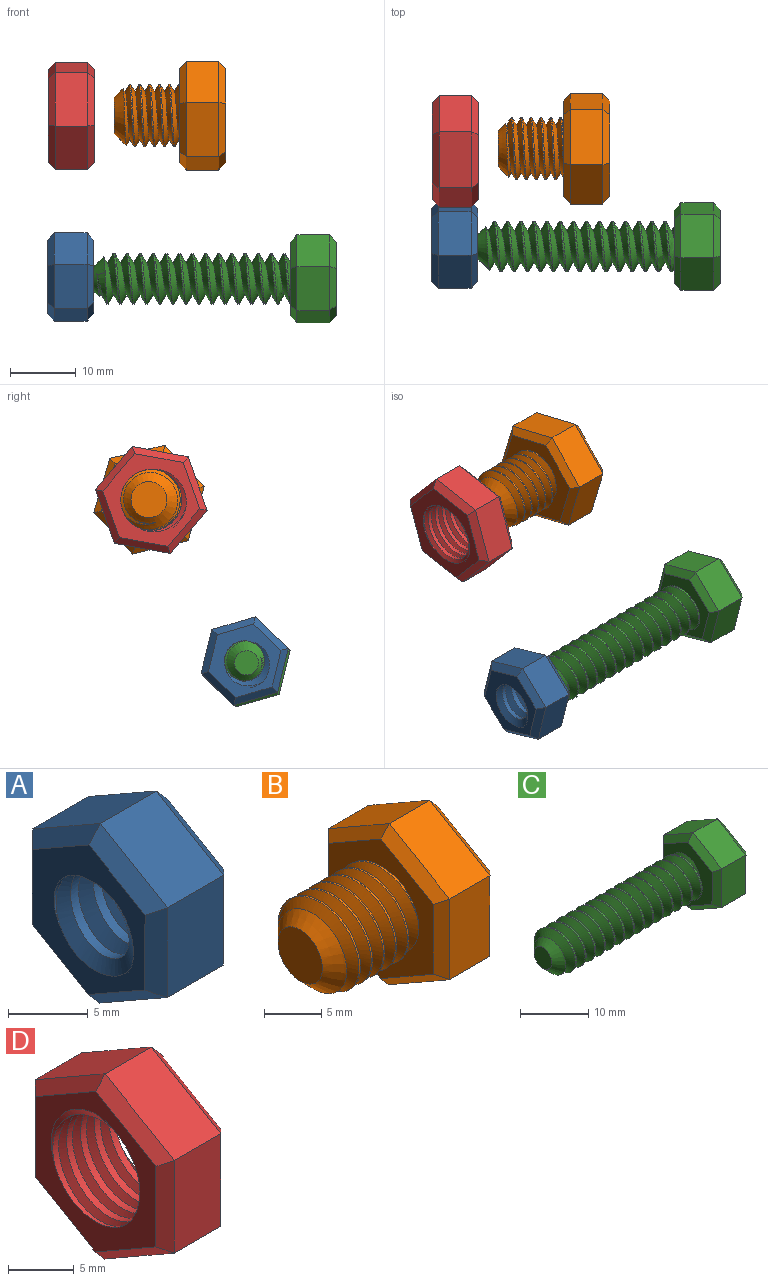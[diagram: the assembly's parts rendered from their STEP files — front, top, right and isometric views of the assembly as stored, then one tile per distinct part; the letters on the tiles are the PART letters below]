
ASSEMBLY  parts=4 mates=2
PART A: 23 faces, bbox 9.2x12.6x14.4 mm
  f0: cylinder r=3.08mm len=7mm, axis (1,0,0), area 47.4mm2, adj f7,f8,f21,f22
  f1: plane 6.02x5mm, normal (0,0.5,0.87), area 34.6mm2, adj f2,f6,f13,f20
  f2: plane 5.98x5mm, normal (0,-0.5,0.86), area 34.6mm2, adj f1,f3,f14,f18
  f3: plane 6.93x5mm, normal (0,-1,-0.01), area 34.6mm2, adj f2,f4,f12,f16
  f4: plane 6.02x5mm, normal (0,-0.5,-0.87), area 34.6mm2, adj f3,f5,f10,f15
  f5: plane 5.98x5mm, normal (0,0.5,-0.86), area 34.6mm2, adj f4,f6,f9,f17
  f6: plane 6.93x5mm, normal (0,1,0.01), area 34.6mm2, adj f1,f5,f11,f19
  f7: plane 12.14x10.62mm, normal (-1,0,0), area 48.9mm2, adj f0,f9,f10,f11,f12,f13,f14,f21
  f8: plane 12.14x10.62mm, normal (1,0,0), area 48.9mm2, adj f0,f15,f16,f17,f18,f19,f20,f21
  f9: plane 5.99x4.07mm, normal (-0.71,0.36,-0.61), area 9mm2, adj f5,f7,f10,f11
  f10: plane 6.02x4.02mm, normal (-0.71,-0.35,-0.61), area 9mm2, adj f4,f7,f9,f12
  f11: plane 6.93x1.03mm, normal (-0.71,0.71,0), area 9mm2, adj f6,f7,f9,f13
  f12: plane 6.93x1.03mm, normal (-0.71,-0.71,0), area 9mm2, adj f3,f7,f10,f14
  f13: plane 6.02x4.02mm, normal (-0.71,0.35,0.61), area 9mm2, adj f1,f7,f11,f14
  f14: plane 5.99x4.07mm, normal (-0.71,-0.36,0.61), area 9mm2, adj f2,f7,f12,f13
  f15: plane 6.02x4.02mm, normal (0.71,-0.35,-0.61), area 9mm2, adj f4,f8,f16,f17
  f16: plane 6.93x1.03mm, normal (0.71,-0.71,0), area 9mm2, adj f3,f8,f15,f18
  f17: plane 5.99x4.07mm, normal (0.71,0.36,-0.61), area 9mm2, adj f5,f8,f15,f19
  f18: plane 5.99x4.07mm, normal (0.71,-0.36,0.61), area 9mm2, adj f2,f8,f16,f20
  f19: plane 6.93x1.03mm, normal (0.71,0.71,0), area 9mm2, adj f6,f8,f17,f20
  f20: plane 6.02x4.02mm, normal (0.71,0.35,0.61), area 9mm2, adj f1,f8,f18,f19
  f21: bspline ~9.71x8.65mm, area 104.3mm2, adj f0,f7,f8,f22
  f22: bspline ~9.71x8.41mm, area 104.3mm2, adj f0,f7,f8,f21
PART B: 25 faces, bbox 17.8x15.9x18.1 mm
  f0: cylinder r=4.75mm len=9.5mm, axis (1,0,0), area 28.1mm2, adj f1,f2,f4,f12
  f1: bspline ~10.97x9.91mm, area 196.7mm2, adj f0,f2,f4,f12
  f2: bspline ~10.97x10.66mm, area 196.6mm2, adj f0,f1,f4,f12
  f3: plane 5.5x5.5mm, normal (-1,0,0), area 23.8mm2, adj f4
  f4: cone r=4.75mm half-angle=45deg, axis (1,0,0), area 47.4mm2, adj f0,f1,f2,f3
  f5: plane 7.48x5mm, normal (0,-0.5,0.86), area 43.3mm2, adj f6,f10,f18,f22
  f6: plane 8.66x5mm, normal (0,-1,0), area 43.3mm2, adj f5,f7,f16,f20
  f7: plane 7.52x5mm, normal (0,-0.5,-0.87), area 43.3mm2, adj f6,f8,f14,f19
  f8: plane 7.48x5mm, normal (0,0.5,-0.86), area 43.3mm2, adj f7,f9,f13,f21
  f9: plane 8.66x5mm, normal (0,1,0), area 43.3mm2, adj f8,f10,f15,f23
  f10: plane 7.52x5mm, normal (0,0.5,0.87), area 43.3mm2, adj f5,f9,f17,f24
  f11: plane 15.01x13.03mm, normal (1,0,0), area 146.4mm2, adj f13,f14,f15,f16,f17,f18
  f12: plane 15.83x13.85mm, normal (-1,0,0), area 89.2mm2, adj f0,f1,f2,f19,f20,f21,f22,f23
  f13: plane 7.49x4.93mm, normal (0.71,0.36,-0.61), area 11.4mm2, adj f8,f11,f14,f15
  f14: plane 7.52x4.88mm, normal (0.71,-0.35,-0.61), area 11.4mm2, adj f7,f11,f13,f16
  f15: plane 8.66x1.03mm, normal (0.71,0.71,0), area 11.4mm2, adj f9,f11,f13,f17
  f16: plane 8.66x1.03mm, normal (0.71,-0.71,0), area 11.4mm2, adj f6,f11,f14,f18
  f17: plane 7.52x4.88mm, normal (0.71,0.35,0.61), area 11.4mm2, adj f10,f11,f15,f18
  f18: plane 7.49x4.93mm, normal (0.71,-0.36,0.61), area 11.4mm2, adj f5,f11,f16,f17
  f19: plane 7.52x4.88mm, normal (-0.71,-0.35,-0.61), area 11.4mm2, adj f7,f12,f20,f21
  f20: plane 8.66x1.03mm, normal (-0.71,-0.71,0), area 11.4mm2, adj f6,f12,f19,f22
  f21: plane 7.49x4.93mm, normal (-0.71,0.36,-0.61), area 11.4mm2, adj f8,f12,f19,f23
  f22: plane 7.49x4.93mm, normal (-0.71,-0.36,0.61), area 11.4mm2, adj f5,f12,f20,f24
  f23: plane 8.66x1.03mm, normal (-0.71,0.71,0), area 11.4mm2, adj f9,f12,f21,f24
  f24: plane 7.52x4.88mm, normal (-0.71,0.35,0.61), area 11.4mm2, adj f10,f12,f22,f23
PART C: 26 faces, bbox 37.7x12x13.9 mm
  f0: cylinder r=3.84mm len=28mm, axis (1,0,0), area 145.1mm2, adj f1,f2,f4,f13
  f1: bspline ~31.88x8.87mm, area 489.8mm2, adj f0,f2,f4,f5,f13
  f2: bspline ~30.88x8.87mm, area 488mm2, adj f0,f1,f4,f5,f13
  f3: plane 3.68x3.68mm, normal (-1,0,0), area 10.6mm2, adj f5
  f4: cone r=3.84mm half-angle=45deg, axis (1,0,0), area 6.1mm2, adj f0,f1,f2,f5
  f5: cone r=3.84mm half-angle=45deg, axis (1,0,0), area 24.7mm2, adj f1,f2,f3,f4
  f6: plane 6.02x5mm, normal (0,0.49,0.87), area 34.6mm2, adj f7,f11,f18,f25
  f7: plane 5.98x5mm, normal (0,-0.51,0.86), area 34.6mm2, adj f6,f8,f19,f23
  f8: plane 6.93x5mm, normal (0,-1,-0.01), area 34.6mm2, adj f7,f9,f17,f21
  f9: plane 6.02x5mm, normal (0,-0.49,-0.87), area 34.6mm2, adj f8,f10,f15,f20
  f10: plane 5.98x5mm, normal (0,0.51,-0.86), area 34.6mm2, adj f9,f11,f14,f22
  f11: plane 6.93x5mm, normal (0,1,0.01), area 34.6mm2, adj f6,f10,f16,f24
  f12: plane 11.55x10.03mm, normal (1,0,0), area 86.6mm2, adj f14,f15,f16,f17,f18,f19
  f13: plane 11.55x10.03mm, normal (-1,0,0), area 54.2mm2, adj f0,f1,f2,f20,f21,f22,f23,f24
  f14: plane 5.99x4.07mm, normal (0.71,0.36,-0.61), area 9mm2, adj f10,f12,f15,f16
  f15: plane 6.02x4.01mm, normal (0.71,-0.35,-0.61), area 9mm2, adj f9,f12,f14,f17
  f16: plane 6.93x1.04mm, normal (0.71,0.71,0), area 9mm2, adj f11,f12,f14,f18
  f17: plane 6.93x1.04mm, normal (0.71,-0.71,0), area 9mm2, adj f8,f12,f15,f19
  f18: plane 6.02x4.01mm, normal (0.71,0.35,0.61), area 9mm2, adj f6,f12,f16,f19
  f19: plane 5.99x4.07mm, normal (0.71,-0.36,0.61), area 9mm2, adj f7,f12,f17,f18
  f20: plane 6.02x4.01mm, normal (-0.71,-0.35,-0.61), area 9mm2, adj f9,f13,f21,f22
  f21: plane 6.93x1.04mm, normal (-0.71,-0.71,0), area 9mm2, adj f8,f13,f20,f23
  f22: plane 5.99x4.07mm, normal (-0.71,0.36,-0.61), area 9mm2, adj f10,f13,f20,f24
  f23: plane 5.99x4.07mm, normal (-0.71,-0.36,0.61), area 9mm2, adj f7,f13,f21,f25
  f24: plane 6.93x1.04mm, normal (-0.71,0.71,0), area 9mm2, adj f11,f13,f22,f25
  f25: plane 6.02x4.01mm, normal (-0.71,0.35,0.61), area 9mm2, adj f6,f13,f23,f24
PART D: 23 faces, bbox 9.1x15.4x17.7 mm
  f0: plane 7.49x5mm, normal (0,-0.5,0.86), area 43.3mm2, adj f1,f5,f13,f17
  f1: plane 8.66x5mm, normal (0,-1,0), area 43.3mm2, adj f0,f2,f11,f15
  f2: plane 7.51x5mm, normal (0,-0.5,-0.87), area 43.3mm2, adj f1,f3,f9,f14
  f3: plane 7.49x5mm, normal (0,0.5,-0.86), area 43.3mm2, adj f2,f4,f8,f16
  f4: plane 8.66x5mm, normal (0,1,0), area 43.3mm2, adj f3,f5,f10,f18
  f5: plane 7.51x5mm, normal (0,0.5,0.87), area 43.3mm2, adj f0,f4,f12,f19
  f6: plane 15.37x13.38mm, normal (-1,0,0), area 71.4mm2, adj f8,f9,f10,f11,f12,f13,f20,f21
  f7: plane 15.37x13.38mm, normal (1,0,0), area 71.4mm2, adj f14,f15,f16,f17,f18,f19,f20,f21
  f8: plane 7.49x4.93mm, normal (-0.71,0.36,-0.61), area 11.4mm2, adj f3,f6,f9,f10
  f9: plane 7.51x4.89mm, normal (-0.71,-0.35,-0.61), area 11.4mm2, adj f2,f6,f8,f11
  f10: plane 8.66x1.02mm, normal (-0.71,0.71,0), area 11.4mm2, adj f4,f6,f8,f12
  f11: plane 8.66x1.02mm, normal (-0.71,-0.71,0), area 11.4mm2, adj f1,f6,f9,f13
  f12: plane 7.51x4.89mm, normal (-0.71,0.35,0.61), area 11.4mm2, adj f5,f6,f10,f13
  f13: plane 7.49x4.93mm, normal (-0.71,-0.36,0.61), area 11.4mm2, adj f0,f6,f11,f12
  f14: plane 7.51x4.89mm, normal (0.71,-0.35,-0.61), area 11.4mm2, adj f2,f7,f15,f16
  f15: plane 8.66x1.02mm, normal (0.71,-0.71,0), area 11.4mm2, adj f1,f7,f14,f17
  f16: plane 7.49x4.93mm, normal (0.71,0.36,-0.61), area 11.4mm2, adj f3,f7,f14,f18
  f17: plane 7.49x4.93mm, normal (0.71,-0.36,0.61), area 11.4mm2, adj f0,f7,f15,f19
  f18: plane 8.66x1.02mm, normal (0.71,0.71,0), area 11.4mm2, adj f4,f7,f16,f19
  f19: plane 7.51x4.89mm, normal (0.71,0.35,0.61), area 11.4mm2, adj f5,f7,f17,f18
  f20: cylinder r=4.66mm len=9.32mm, axis (1,0,0), area 85.4mm2, adj f6,f7,f21,f22
  f21: bspline ~12.5x10.82mm, area 128.4mm2, adj f6,f7,f20,f22
  f22: bspline ~12.5x10.82mm, area 128.5mm2, adj f6,f7,f20,f21
PLACE A rot(axis=(0,0.6,-0.8),180deg) t=(-55.27,-6.86,23.48)mm fixed
PLACE B rot(axis=(-1,0,0),43.8deg) t=(-31.66,7.73,48.08)mm
PLACE C rot(axis=(-1,0,0),106.1deg) t=(-14.77,-7.14,23.19)mm
PLACE D rot(axis=(1,0,0),100.2deg) t=(-48.16,7.38,48.02)mm fixed
MATE cylindrical C.f0 <-> A.f7  axis (-1,0,0) through (-48.27,-7.14,23.19)mm
MATE cylindrical B.f0 <-> D.f6  axis (-1,0,0) through (-45.16,7.73,48.08)mm
